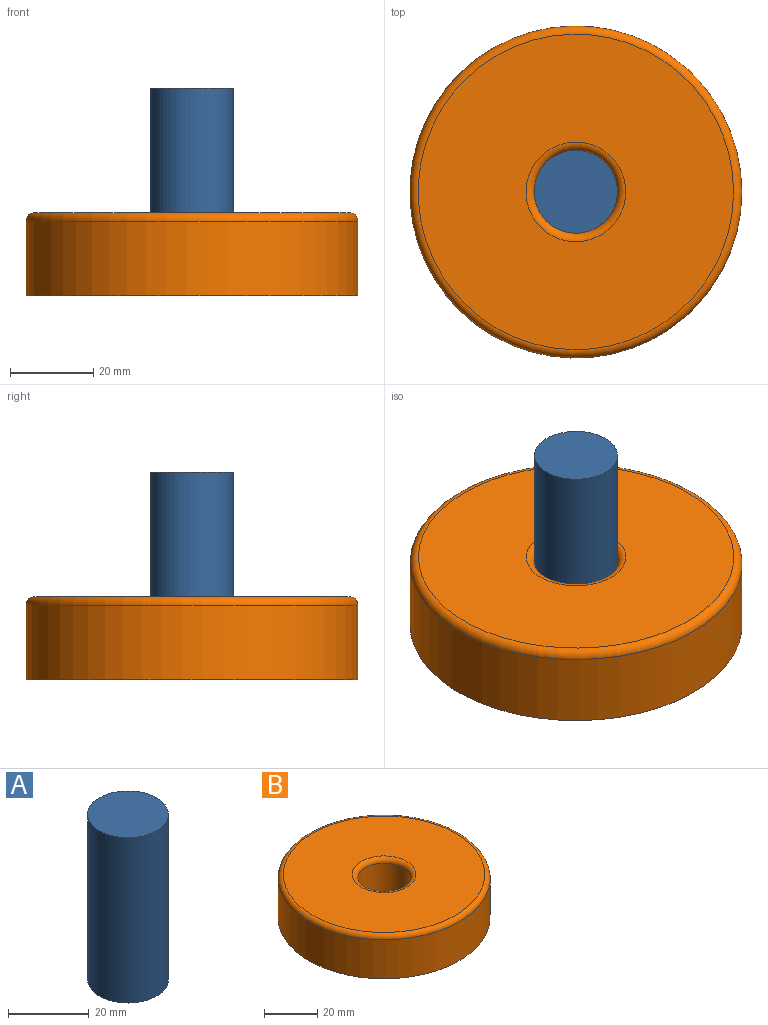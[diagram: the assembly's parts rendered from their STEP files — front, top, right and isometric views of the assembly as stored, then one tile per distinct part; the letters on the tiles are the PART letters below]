
ASSEMBLY  parts=2 mates=1
PART A: 3 faces, bbox 20x20x50 mm
  f0: cylinder r=10mm len=50mm, axis (0,0,-1), area 3141.6mm2, adj f1,f2
  f1: plane 20x20mm, normal (0,0,1), area 314.2mm2, adj f0
  f2: plane 20x20mm, normal (0,0,-1), area 314.2mm2, adj f0
PART B: 6 faces, bbox 86.6x86.6x20 mm
  f0: cylinder r=10mm len=20mm, axis (0,0,-1), area 1131mm2, adj f3,f4
  f1: cylinder r=40mm len=80mm, axis (0,0,-1), area 4523.9mm2, adj f3,f5
  f2: plane 76x76mm, normal (0,0,1), area 4084.1mm2, adj f4,f5
  f3: plane 80x80mm, normal (0,0,-1), area 4712.4mm2, adj f0,f1
  f4: torus R=12mm, axis (0,0,1), area 211.7mm2, adj f0,f2
  f5: torus R=38mm, axis (0,0,1), area 775.2mm2, adj f1,f2
PLACE A t=(13.74,45.71,-9.98)mm
PLACE B t=(13.74,45.71,-9.98)mm fixed
MATE slider A.f0 <-> B.f1  axis (0,0,-1) through (13.74,45.71,40.02)mm
